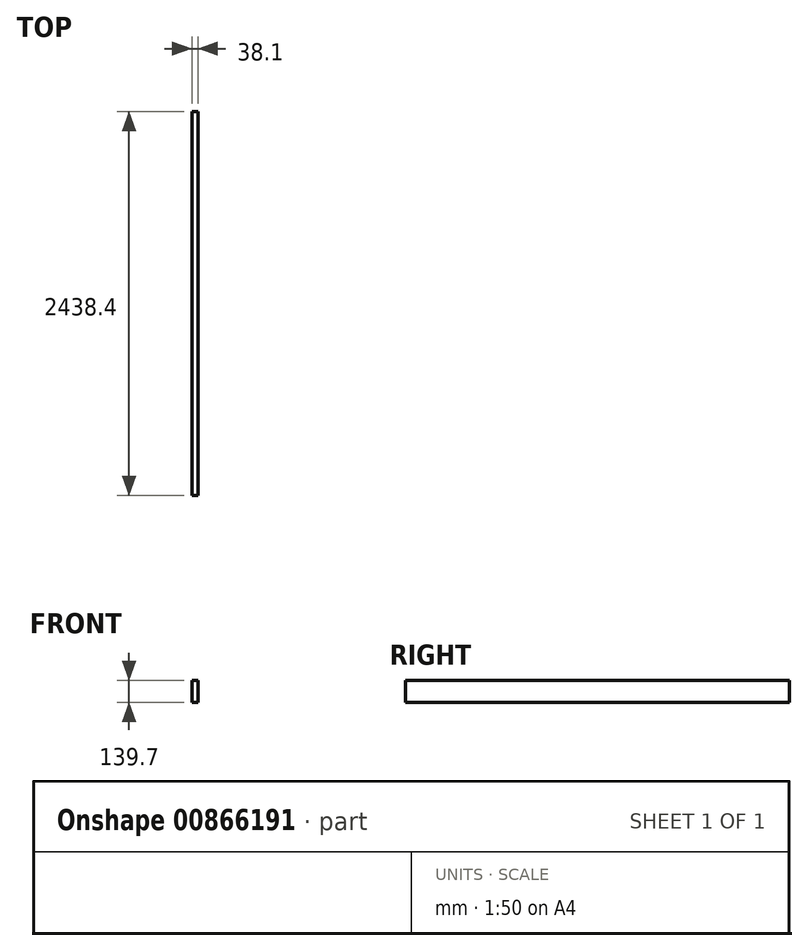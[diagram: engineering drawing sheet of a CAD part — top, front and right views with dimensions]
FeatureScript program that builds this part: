
annotation { "Feature Type Name" : "Feature", "Feature Type Description" : "" }
export const myFeature = defineFeature(function(context is Context, id is Id, definition is map)
    precondition{}
    {
        {
            var Q0;
            Q0=qCreatedBy(makeId("Front.planeOp"),FACE);
            var sketch = newSketch(context, id + "F0", { "sketchPlane" : qUnion([Q0])});
            skLineSegment(sketch, "E0.bottom", {"start": v(-242.03, -22.43) * mm, "end": v(-203.93, -22.43) * mm});
            skLineSegment(sketch, "E0.top", {"start": v(-242.03, -162.13) * mm, "end": v(-203.93, -162.13) * mm});
            skLineSegment(sketch, "E0.left", {"start": v(-242.03, -22.43) * mm, "end": v(-242.03, -162.13) * mm});
            skLineSegment(sketch, "E0.right", {"start": v(-203.93, -22.43) * mm, "end": v(-203.93, -162.13) * mm});
            skSolve(sketch);
        }
        {
            var Q0;
            Q0 = qSketchRegion(id + "F0", true);
            extrude(context, id + "F1", {"entities" : qUnion([Q0]), "oppositeDirection" : true, "depth" : 2438.4 * mm, "offsetDistance" : 25.4 * mm});
        }
    });
